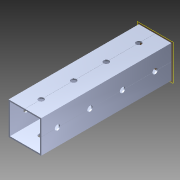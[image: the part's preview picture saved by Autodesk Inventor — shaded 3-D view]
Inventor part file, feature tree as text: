
AUTODESK INVENTOR PART (.ipt)
format: ipt  version: 2014 (Build 180170000, 170)  size: 1,237,504 bytes
history: native  units: in
note: dims shown in document units (in); Inventor stores cm internally (conversion verified against a paired STEP export)
features: extrude x4, sketch x4, pattern_circular x1, other x1, plane x1, imported_body x1
ambient origin geometry x8: Origin, YZ Plane, XZ Plane, XY Plane, X Axis, Y Axis, Z Axis, Center Point
bodies: Body1 (feature_tree)
feature tree (12):
  pattern_circular  "CirPattern2"
  other  "217-3426-STEP1"
  plane  "Work Plane1"
  extrude  "Extrusion1"  Depth=3937.0079in TaperAngle=0.0deg
  extrude  "Extrusion2"  Depth=1.0in TaperAngle=0.0deg
  extrude  "Extrusion3"  Depth=0.3937in TaperAngle=0.0deg
  extrude  "Extrusion5"  [1 undecoded]
  imported_body  "Base1"
  sketch  "Sketch1"  dims[d0=-21.0in d1=3937.0079in d2=0.0in]
  sketch  "Sketch3"  dims[d3=1.0in d4=0.0in d5=16.0in d6=0.0in]
  sketch  "Sketch4"  dims[d10=0.196in d11=0.3937in d12=0.0in]
  sketch  "Sketch6"
note: 1 required parameter value undecoded (feature->parameter linkage not recoverable at this tier; creation-order binding heuristic only, values carry confidence <= 0.55)
